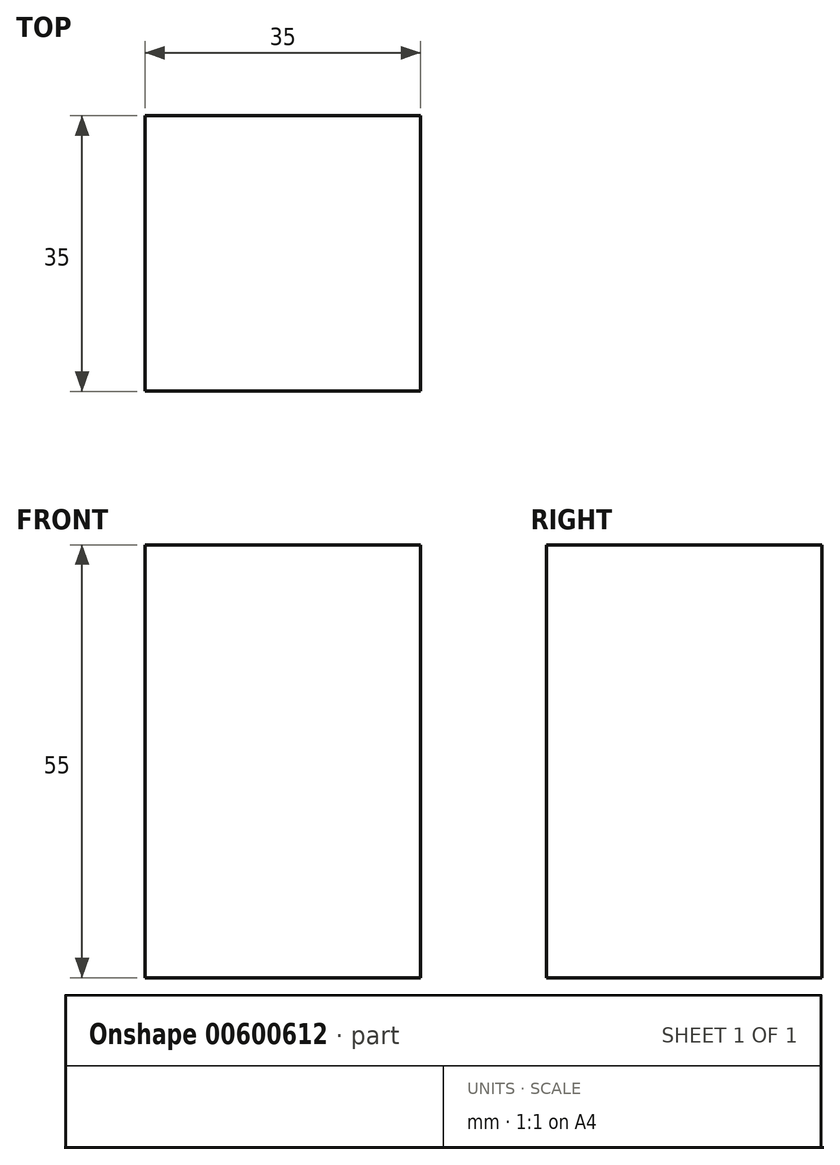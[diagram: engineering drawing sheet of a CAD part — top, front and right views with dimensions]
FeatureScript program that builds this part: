
annotation { "Feature Type Name" : "Feature", "Feature Type Description" : "" }
export const myFeature = defineFeature(function(context is Context, id is Id, definition is map)
    precondition{}
    {
        {
            var Q0;
            Q0=qCreatedBy(makeId("Top.planeOp"),FACE);
            var sketch = newSketch(context, id + "F0", { "sketchPlane" : qUnion([Q0])});
            skLineSegment(sketch, "E0.bottom", {"start": v(-21.63, 18.4) * mm, "end": v(13.37, 18.4) * mm});
            skLineSegment(sketch, "E0.top", {"start": v(-21.63, -16.6) * mm, "end": v(13.37, -16.6) * mm});
            skLineSegment(sketch, "E0.left", {"start": v(-21.63, 18.4) * mm, "end": v(-21.63, -16.6) * mm});
            skLineSegment(sketch, "E0.right", {"start": v(13.37, 18.4) * mm, "end": v(13.37, -16.6) * mm});
            skSolve(sketch);
        }
        {
            var Q0;
            Q0=makeQuery(id+"F0.imprint","IMPRINT",FACE,{"disambiguationData":[TD([[makeQuery(id+"F0.imprint","IMPRINT",EDGE,{"derivedFrom":sQuery(id+"F0.wireOp",EDGE,"E0.bottom")}),-1.0]])]});
            extrude(context, id + "F1", {"entities" : qUnion([Q0]), "depth" : 55 * mm, "offsetDistance" : 25 * mm});
        }
    });
